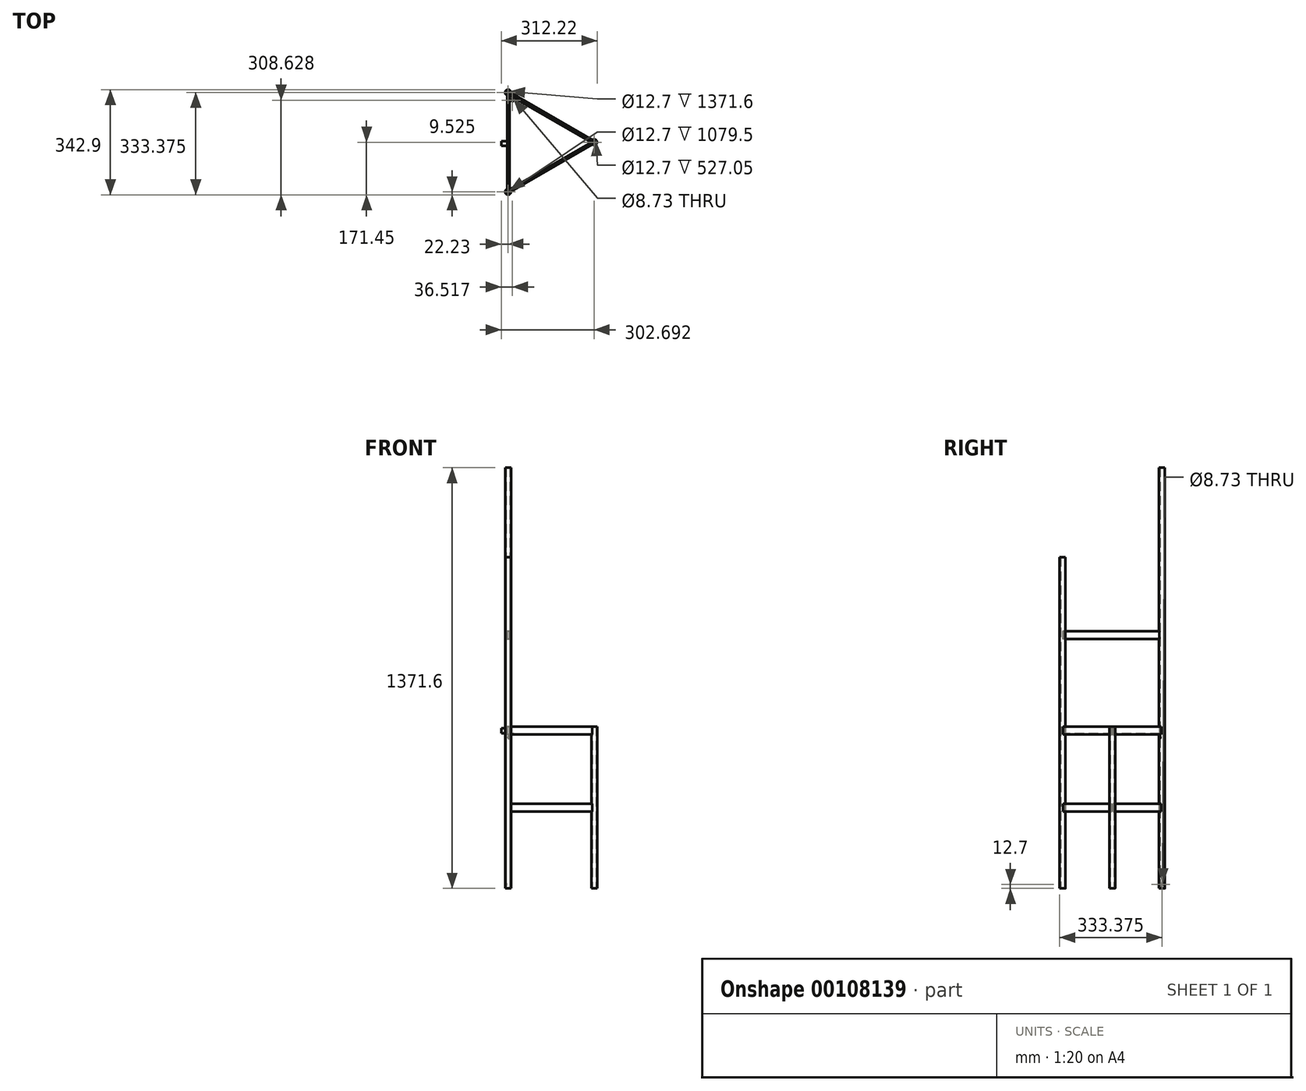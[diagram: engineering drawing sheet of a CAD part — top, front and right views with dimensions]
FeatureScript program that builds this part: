
annotation { "Feature Type Name" : "Feature", "Feature Type Description" : "" }
export const myFeature = defineFeature(function(context is Context, id is Id, definition is map)
    precondition{}
    {
        {
            var Q0;
            Q0=qCreatedBy(makeId("Top.planeOp"),FACE);
            var sketch = newSketch(context, id + "F0", { "sketchPlane" : qUnion([Q0])});
            skLineSegment(sketch, "E0.0", {"start": v(280.46, 0) * mm, "end": v(0, -161.92) * mm, "construction": true});
            skLineSegment(sketch, "E0.1", {"start": v(0, -161.93) * mm, "end": v(0, 161.92) * mm, "construction": true});
            skLineSegment(sketch, "E0.2", {"start": v(0, 161.93) * mm, "end": v(280.46, 0) * mm, "construction": true});
            skPoint(sketch, "E0.0.midPoint", {"position": v(140.23, -80.96) * mm});
            skCircle(sketch, "E1", {"center": v(0, 161.92) * mm, "radius": 9.52 * mm, "construction": true});
            skCircle(sketch, "E2", {"center": v(280.46, 0) * mm, "radius": 9.52 * mm, "construction": true});
            skCircle(sketch, "E3", {"center": v(0, -161.92) * mm, "radius": 9.52 * mm, "construction": true});
            skLineSegment(sketch, "E4", {"start": v(0, 0) * mm, "end": v(280.46, 0) * mm, "construction": true});
            skPoint(sketch, "E5", {"position": v(140.23, 80.96) * mm});
            skPoint(sketch, "E6", {"position": v(0, -152.4) * mm});
            skPoint(sketch, "E7", {"position": v(0, 152.4) * mm});
            skPoint(sketch, "E8", {"position": v(8.25, -157.16) * mm});
            skPoint(sketch, "E9", {"position": v(272.21, -4.76) * mm});
            skLineSegment(sketch, "E10", {"start": v(0, -161.92) * mm, "end": v(0, -171.45) * mm, "construction": true});
            skLineSegment(sketch, "E11", {"start": v(0, 161.92) * mm, "end": v(140.23, -80.96) * mm, "construction": true});
            skSolve(sketch);
        }
        {
            var Q0;
            Q0=qCreatedBy(makeId("Top.planeOp"),FACE);
            var sketch = newSketch(context, id + "F1", { "sketchPlane" : qUnion([Q0])});
            skCircle(sketch, "E12", {"center": v(0, 161.92) * mm, "radius": 9.52 * mm});
            skCircle(sketch, "E13.0", {"center": v(0, 161.92) * mm, "radius": 6.35 * mm});
            skSolve(sketch);
        }
        {
            var Q0;
            Q0 = qSketchRegion(id + "F1", true);
            extrude(context, id + "F2", {"entities" : qUnion([Q0]), "depth" : 1371.6 * mm});
        }
        {
            var Q0;
            Q0=qCreatedBy(makeId("Top.planeOp"),FACE);
            var sketch = newSketch(context, id + "F3", { "sketchPlane" : qUnion([Q0])});
            skCircle(sketch, "E14", {"center": v(0, -161.92) * mm, "radius": 9.52 * mm});
            skCircle(sketch, "E15.0", {"center": v(0, -161.92) * mm, "radius": 6.35 * mm});
            skSolve(sketch);
        }
        {
            var Q0;
            Q0 = qSketchRegion(id + "F3", true);
            extrude(context, id + "F4", {"entities" : qUnion([Q0]), "depth" : 1079.5 * mm});
        }
        {
            var Q0;
            Q0=qCreatedBy(makeId("Top.planeOp"),FACE);
            var sketch = newSketch(context, id + "F5", { "sketchPlane" : qUnion([Q0])});
            skCircle(sketch, "E16", {"center": v(280.46, 0) * mm, "radius": 9.52 * mm});
            skCircle(sketch, "E17.0", {"center": v(280.46, 0) * mm, "radius": 6.35 * mm});
            skSolve(sketch);
        }
        {
            var Q0;
            Q0 = qSketchRegion(id + "F5", true);
            extrude(context, id + "F6", {"entities" : qUnion([Q0]), "depth" : 527.05 * mm});
        }
        {
            var Q0;
            Q0=makeQuery(id+"F2.opExtrude","CAP_FACE",FACE,{"disambiguationData":[OSD([sQuery(id+"F1.wireOp",EDGE,"E12")])],"isStart":false});
            cPlane(context, id + "F7", {"entities" : qUnion([Q0]), "cplaneType" : CPlaneType.OFFSET, "offset" : 101.6 * mm, "width" : 152.4 * mm, "height" : 152.4 * mm});
        }
        {
            var Q0;
            Q0=qCreatedBy(id+"F7.planeOp",FACE);
            var sketch = newSketch(context, id + "F8", { "sketchPlane" : qUnion([Q0])});
            skArc(sketch, "E18", {"start": v(127, 161.92) * mm, "mid": v(0, 288.93) * mm, "end": v(-127, 161.93) * mm});
            skLineSegment(sketch, "E19", {"start": v(-127, 161.92) * mm, "end": v(127, 161.92) * mm});
            skLineSegment(sketch, "E20", {"start": v(127, 161.92) * mm, "end": v(165.16, 161.92) * mm, "construction": true});
            skSolve(sketch);
        }
        {
            var Q0;
            Q0 = qSketchRegion(id + "F8", true);
            var Q1;
            Q1=sQuery(id+"F8.wireOp",EDGE,"E19");
            revolve(context, id + "F9", {"entities" : qUnion([Q0]), "axis" : qUnion([Q1]), "revolveType" : RevolveType.FULL});
        }
        {
            var Q0;
            Q0=makeQuery(id+"F6.opExtrude","CAP_FACE",FACE,{"disambiguationData":[OSD([sQuery(id+"F5.wireOp",EDGE,"E16")])],"isStart":false});
            var sketch = newSketch(context, id + "F10", { "sketchPlane" : qUnion([Q0])});
            skCircle(sketch, "E21", {"center": v(156.83, 0) * mm, "radius": 215.9 * mm});
            skLineSegment(sketch, "E22.0", {"start": v(0, -161.93) * mm, "end": v(0, 161.92) * mm, "construction": true});
            skLineSegment(sketch, "E23", {"start": v(0, 0) * mm, "end": v(280.46, 0) * mm, "construction": true});
            skCircle(sketch, "E24.0", {"center": v(0, 161.92) * mm, "radius": 9.52 * mm, "construction": true});
            skSolve(sketch);
        }
        {
            var Q0;
            Q0 = qSketchRegion(id + "F10", true);
            extrude(context, id + "F11", {"entities" : qUnion([Q0]), "depth" : 19.05 * mm});
        }
        {
            var Q0;
            Q0=makeQuery(id+"F4.opExtrude","CAP_FACE",FACE,{"disambiguationData":[OSD([sQuery(id+"F3.wireOp",EDGE,"E14")])],"isStart":false});
            var sketch = newSketch(context, id + "F12", { "sketchPlane" : qUnion([Q0])});
            skLineSegment(sketch, "E25", {"start": v(0, -161.92) * mm, "end": v(0, -171.45) * mm, "construction": true});
            skLineSegment(sketch, "E26", {"start": v(0, -171.45) * mm, "end": v(0, -199.27) * mm, "construction": true});
            skSolve(sketch);
        }
        {
            var Q0;
            Q0=qCreatedBy(makeId("Right.planeOp"),FACE);
            var sketch = newSketch(context, id + "F13", { "sketchPlane" : qUnion([Q0])});
            skLineSegment(sketch, "E27.0", {"start": v(-161.92, 1079.5) * mm, "end": v(-171.45, 1079.5) * mm, "construction": true});
            skLineSegment(sketch, "E28", {"start": v(-72.12, 989.7) * mm, "end": v(-251.73, 1169.3) * mm});
            skLineSegment(sketch, "E29", {"start": v(-251.73, 1169.3) * mm, "end": v(-220.3, 1200.73) * mm});
            skLineSegment(sketch, "E30", {"start": v(-220.3, 1200.73) * mm, "end": v(-40.7, 1021.13) * mm});
            skLineSegment(sketch, "E31", {"start": v(-40.7, 1021.13) * mm, "end": v(-72.12, 989.7) * mm});
            skSolve(sketch);
        }
        {
            var Q0;
            Q0 = qSketchRegion(id + "F13", true);
            var Q1;
            Q1=sQuery(id+"F13.wireOp",EDGE,"E30");
            revolve(context, id + "F14", {"entities" : qUnion([Q0]), "axis" : qUnion([Q1]), "revolveType" : RevolveType.FULL});
        }
        {
            var Q0;
            Q0=qCreatedBy(makeId("Front.planeOp"),FACE);
            var Q1;
            Q1=sQuery(id+"F0.wireOp",VERTEX,"E10.start");
            cPlane(context, id + "F15", {"entities" : qUnion([Q0, Q1]), "cplaneType" : CPlaneType.PLANE_POINT, "offset" : 25.4 * mm, "width" : 152.4 * mm, "height" : 152.4 * mm});
        }
        {
            var Q0;
            Q0=qCreatedBy(id+"F15.planeOp",FACE);
            var sketch = newSketch(context, id + "F16", { "sketchPlane" : qUnion([Q0])});
            skLineSegment(sketch, "E32", {"start": v(0, 0) * mm, "end": v(0, -94.54) * mm, "construction": true});
            skSolve(sketch);
        }
        {
            var Q0;
            Q0=makeQuery(id+"F14.opRevolve","SWEPT_BODY",BODY,{"disambiguationData":[OSD([sQuery(id+"F13.wireOp",EDGE,"E28"),sQuery(id+"F13.wireOp",EDGE,"E29"),sQuery(id+"F13.wireOp",EDGE,"E30"),sQuery(id+"F13.wireOp",EDGE,"E31")])]});
            var Q1;
            Q1=sQuery(id+"F16.wireOp",EDGE,"E32");
            transform(context, id + "F17", {"entities" : qUnion([Q0]), "transformType" : TransformType.ROTATION, "transformAxis" : qUnion([Q1]), "angle" : 125 * degree, "makeCopy" : false});
        }
        {
            var Q0;
            Q0=qCreatedBy(makeId("Front.planeOp"),FACE);
            var sketch = newSketch(context, id + "F18", { "sketchPlane" : qUnion([Q0])});
            skCircle(sketch, "E33", {"center": v(0, 263.53) * mm, "radius": 9.53 * mm});
            skLineSegment(sketch, "E34", {"start": v(0, 0) * mm, "end": v(0, 527.05) * mm, "construction": true});
            skLineSegment(sketch, "E35.0", {"start": v(-59.07, 527.05) * mm, "end": v(372.73, 527.05) * mm, "construction": true});
            skSolve(sketch);
        }
        {
            var Q0;
            Q0 = qSketchRegion(id + "F18", true);
            var Q1;
            Q1=makeQuery(id+"F4.opExtrude","SWEPT_FACE",FACE,{"disambiguationData":[OSD([sQuery(id+"F3.wireOp",EDGE,"E14")])]});
            var Q2;
            Q2=makeQuery(id+"F2.opExtrude","SWEPT_FACE",FACE,{"disambiguationData":[OSD([sQuery(id+"F1.wireOp",EDGE,"E12")])]});
            extrude(context, id + "F19", {"entities" : qUnion([Q0]), "endBound" : BoundingType.UP_TO_SURFACE, "endBoundEntityFace" : qUnion([Q1]), "depth" : 25.4 * mm, "hasSecondDirection" : true, "secondDirectionBound" : BoundingType.UP_TO_SURFACE, "secondDirectionOppositeDirection" : true, "secondDirectionBoundEntityFace" : qUnion([Q2]), "secondDirectionDepth" : 25.4 * mm});
        }
        {
            var Q0;
            Q0=makeQuery(id+"F6.opExtrude","CAP_FACE",FACE,{"disambiguationData":[OSD([sQuery(id+"F5.wireOp",EDGE,"E16")])],"isStart":false});
            var sketch = newSketch(context, id + "F20", { "sketchPlane" : qUnion([Q0])});
            skCircle(sketch, "E36.0", {"center": v(280.46, 0) * mm, "radius": 9.52 * mm, "construction": true});
            skSolve(sketch);
        }
        {
            var Q0;
            Q0=sQuery(id+"F0.wireOp",EDGE,"E0.0");
            var Q1;
            Q1=sQuery(id+"F0.wireOp",VERTEX,"E0.0.midPoint");
            cPlane(context, id + "F21", {"entities" : qUnion([Q0, Q1]), "cplaneType" : CPlaneType.LINE_POINT, "offset" : 25.4 * mm, "width" : 152.4 * mm, "height" : 152.4 * mm});
        }
        {
            var Q0;
            Q0=sQuery(id+"F0.wireOp",EDGE,"E0.2");
            var Q1;
            Q1=sQuery(id+"F0.wireOp",VERTEX,"E5");
            cPlane(context, id + "F22", {"entities" : qUnion([Q0, Q1]), "cplaneType" : CPlaneType.LINE_POINT, "offset" : 25.4 * mm, "width" : 152.4 * mm, "height" : 152.4 * mm});
        }
        {
            var Q0;
            Q0=qCreatedBy(id+"F21.planeOp",FACE);
            var sketch = newSketch(context, id + "F23", { "sketchPlane" : qUnion([Q0])});
            skCircle(sketch, "E37", {"center": v(140.23, 263.53) * mm, "radius": 9.53 * mm, "construction": true});
            skLineSegment(sketch, "E38", {"start": v(140.23, 0) * mm, "end": v(140.23, 527.05) * mm, "construction": true});
            skLineSegment(sketch, "E39.bottom", {"start": v(143.4, 276.23) * mm, "end": v(137.06, 276.23) * mm});
            skLineSegment(sketch, "E39.top", {"start": v(143.4, 250.83) * mm, "end": v(137.06, 250.83) * mm});
            skLineSegment(sketch, "E39.left", {"start": v(143.4, 276.23) * mm, "end": v(143.4, 250.83) * mm});
            skLineSegment(sketch, "E39.right", {"start": v(137.06, 276.23) * mm, "end": v(137.06, 250.83) * mm});
            skLineSegment(sketch, "E40", {"start": v(137.06, 276.23) * mm, "end": v(143.4, 250.83) * mm, "construction": true});
            skLineSegment(sketch, "E41.bottom", {"start": v(137.06, 501.65) * mm, "end": v(143.4, 501.65) * mm});
            skLineSegment(sketch, "E41.top", {"start": v(137.06, 527.05) * mm, "end": v(143.4, 527.05) * mm});
            skLineSegment(sketch, "E41.left", {"start": v(137.06, 501.65) * mm, "end": v(137.06, 527.05) * mm});
            skLineSegment(sketch, "E41.right", {"start": v(143.4, 501.65) * mm, "end": v(143.4, 527.05) * mm});
            skPoint(sketch, "E41.middle", {"position": v(140.23, 514.35) * mm});
            skSolve(sketch);
        }
        {
            var Q0;
            Q0 = qSketchRegion(id + "F23", true);
            var Q1;
            Q1=makeQuery(id+"F4.opExtrude","SWEPT_FACE",FACE,{"disambiguationData":[OSD([sQuery(id+"F3.wireOp",EDGE,"E14")])]});
            var Q2;
            Q2=makeQuery(id+"F6.opExtrude","SWEPT_FACE",FACE,{"disambiguationData":[OSD([sQuery(id+"F5.wireOp",EDGE,"E16")])]});
            extrude(context, id + "F24", {"entities" : qUnion([Q0]), "endBound" : BoundingType.UP_TO_SURFACE, "endBoundEntityFace" : qUnion([Q1]), "depth" : 25.4 * mm, "hasSecondDirection" : true, "secondDirectionBound" : BoundingType.UP_TO_SURFACE, "secondDirectionOppositeDirection" : true, "secondDirectionBoundEntityFace" : qUnion([Q2]), "secondDirectionDepth" : 25.4 * mm});
        }
        {
            var Q0;
            Q0=qCreatedBy(id+"F22.planeOp",FACE);
            var sketch = newSketch(context, id + "F25", { "sketchPlane" : qUnion([Q0])});
            skLineSegment(sketch, "E42", {"start": v(140.23, 0) * mm, "end": v(140.23, 527.05) * mm, "construction": true});
            skCircle(sketch, "E43", {"center": v(140.23, 263.53) * mm, "radius": 9.53 * mm, "construction": true});
            skLineSegment(sketch, "E44.bottom", {"start": v(137.06, 250.83) * mm, "end": v(143.4, 250.83) * mm});
            skLineSegment(sketch, "E44.top", {"start": v(137.06, 276.23) * mm, "end": v(143.4, 276.23) * mm});
            skLineSegment(sketch, "E44.left", {"start": v(137.06, 250.83) * mm, "end": v(137.06, 276.23) * mm});
            skLineSegment(sketch, "E44.right", {"start": v(143.4, 250.83) * mm, "end": v(143.4, 276.23) * mm});
            skLineSegment(sketch, "E45", {"start": v(143.4, 276.23) * mm, "end": v(137.06, 250.83) * mm, "construction": true});
            skLineSegment(sketch, "E46.bottom", {"start": v(143.4, 527.05) * mm, "end": v(137.06, 527.05) * mm});
            skLineSegment(sketch, "E46.top", {"start": v(143.4, 501.65) * mm, "end": v(137.06, 501.65) * mm});
            skLineSegment(sketch, "E46.left", {"start": v(143.4, 527.05) * mm, "end": v(143.4, 501.65) * mm});
            skLineSegment(sketch, "E46.right", {"start": v(137.06, 527.05) * mm, "end": v(137.06, 501.65) * mm});
            skPoint(sketch, "E46.middle", {"position": v(140.23, 514.35) * mm});
            skSolve(sketch);
        }
        {
            var Q0;
            Q0 = qSketchRegion(id + "F25", true);
            var Q1;
            Q1=makeQuery(id+"F6.opExtrude","SWEPT_FACE",FACE,{"disambiguationData":[OSD([sQuery(id+"F5.wireOp",EDGE,"E16")])]});
            var Q2;
            Q2=makeQuery(id+"F2.opExtrude","SWEPT_FACE",FACE,{"disambiguationData":[OSD([sQuery(id+"F1.wireOp",EDGE,"E12")])]});
            extrude(context, id + "F26", {"entities" : qUnion([Q0]), "endBound" : BoundingType.UP_TO_SURFACE, "endBoundEntityFace" : qUnion([Q1]), "depth" : 25.4 * mm, "hasSecondDirection" : true, "secondDirectionBound" : BoundingType.UP_TO_SURFACE, "secondDirectionOppositeDirection" : true, "secondDirectionBoundEntityFace" : qUnion([Q2]), "secondDirectionDepth" : 25.4 * mm});
        }
        {
            var Q0;
            Q0=makeQuery(id+"F24.opExtrude","SWEPT_FACE",FACE,{"disambiguationData":[OSD([sQuery(id+"F23.wireOp",EDGE,"E41.bottom")])]});
            var sketch = newSketch(context, id + "F27", { "sketchPlane" : qUnion([Q0])});
            skLineSegment(sketch, "E47.0", {"start": v(280.46, 0) * mm, "end": v(0, 161.92) * mm, "construction": true});
            skLineSegment(sketch, "E47.1", {"start": v(0, -161.93) * mm, "end": v(280.46, 0) * mm, "construction": true});
            skLineSegment(sketch, "E47.2", {"start": v(0, 161.93) * mm, "end": v(0, -161.92) * mm, "construction": true});
            skLineSegment(sketch, "E48.0", {"start": v(270.94, 0) * mm, "end": v(4.76, 153.68) * mm});
            skLineSegment(sketch, "E48.1", {"start": v(4.76, -153.68) * mm, "end": v(270.94, 0) * mm});
            skLineSegment(sketch, "E48.2", {"start": v(4.76, 153.68) * mm, "end": v(4.76, -153.68) * mm});
            skCircle(sketch, "E49.0", {"center": v(0, 161.92) * mm, "radius": 9.52 * mm, "construction": true});
            skCircle(sketch, "E49.1", {"center": v(280.46, 0) * mm, "radius": 9.52 * mm, "construction": true});
            skCircle(sketch, "E49.2", {"center": v(0, -161.92) * mm, "radius": 9.52 * mm, "construction": true});
            skSolve(sketch);
        }
        {
            var Q0;
            {var subQ0=sQuery(id+"F27.wireOp",EDGE,"E48.0");var subQ5=sQuery(id+"F27.wireOp",EDGE,"E48.1");var subQ6=makeQuery(id+"F27.imprint","INTERSECT",VERTEX,{"derivedFrom":[subQ0,subQ5]});Q0=makeQuery(id+"F27.imprint","IMPRINT",FACE,{"disambiguationData":[TD([[makeQuery(id+"F27.imprint","IMPRINT",EDGE,{"disambiguationData":[TD([[subQ6,-1.0]])],"derivedFrom":subQ0}),1.0]])]});}
            extrude(context, id + "F28", {"entities" : qUnion([Q0]), "oppositeDirection" : true, "depth" : 3.17 * mm});
        }
        {
            var Q0;
            Q0=qCreatedBy(id+"F15.planeOp",FACE);
            var sketch = newSketch(context, id + "F29", { "sketchPlane" : qUnion([Q0])});
            skLineSegment(sketch, "E50.0", {"start": v(-9.53, 0) * mm, "end": v(9.52, 0) * mm, "construction": true});
            skLineSegment(sketch, "E51", {"start": v(-9.53, 0) * mm, "end": v(-9.53, 527.05) * mm, "construction": true});
            skLineSegment(sketch, "E52.0", {"start": v(-59.07, 527.05) * mm, "end": v(372.73, 527.05) * mm, "construction": true});
            skLineSegment(sketch, "E53", {"start": v(9.52, 0) * mm, "end": v(9.52, 527.05) * mm, "construction": true});
            skCircle(sketch, "E54", {"center": v(0, 517.52) * mm, "radius": 9.52 * mm, "construction": true});
            skLineSegment(sketch, "E55.bottom", {"start": v(3.17, 527.05) * mm, "end": v(-3.18, 527.05) * mm});
            skLineSegment(sketch, "E55.top", {"start": v(3.17, 501.65) * mm, "end": v(-3.18, 501.65) * mm});
            skLineSegment(sketch, "E55.left", {"start": v(-3.18, 501.65) * mm, "end": v(-3.18, 527.05) * mm});
            skLineSegment(sketch, "E55.right", {"start": v(3.17, 501.65) * mm, "end": v(3.17, 527.05) * mm});
            skPoint(sketch, "E55.middle", {"position": v(0, 514.35) * mm});
            skSolve(sketch);
        }
        {
            var Q0;
            Q0 = qSketchRegion(id + "F29", true);
            var Q1;
            Q1=makeQuery(id+"F2.opExtrude","SWEPT_FACE",FACE,{"disambiguationData":[OSD([sQuery(id+"F1.wireOp",EDGE,"E12")])]});
            extrude(context, id + "F30", {"entities" : qUnion([Q0]), "endBound" : BoundingType.UP_TO_SURFACE, "oppositeDirection" : true, "endBoundEntityFace" : qUnion([Q1]), "depth" : 25.4 * mm});
        }
        {
            var Q0;
            Q0=qCreatedBy(makeId("Right.planeOp"),FACE);
            var sketch = newSketch(context, id + "F31", { "sketchPlane" : qUnion([Q0])});
            skLineSegment(sketch, "E56.0", {"start": v(152.4, 1371.6) * mm, "end": v(171.45, 1371.6) * mm, "construction": true});
            skLineSegment(sketch, "E57.bottom", {"start": v(104.77, 1381.13) * mm, "end": v(219.07, 1381.13) * mm, "construction": true});
            skLineSegment(sketch, "E57.top", {"start": v(104.77, 1371.6) * mm, "end": v(219.08, 1371.6) * mm, "construction": true});
            skLineSegment(sketch, "E57.left", {"start": v(104.77, 1381.13) * mm, "end": v(104.77, 1371.6) * mm, "construction": true});
            skLineSegment(sketch, "E57.right", {"start": v(219.07, 1381.13) * mm, "end": v(219.07, 1371.6) * mm, "construction": true});
            skPoint(sketch, "E58", {"position": v(161.92, 1371.6) * mm});
            skCircle(sketch, "E59", {"center": v(161.92, 1494.54) * mm, "radius": 127 * mm, "construction": true});
            skPoint(sketch, "E59.centerSnap0", {"position": v(161.92, 1381.13) * mm});
            skSolve(sketch);
        }
        {
            var Q0;
            Q0=qCreatedBy(makeId("Right.planeOp"),FACE);
            var sketch = newSketch(context, id + "F32", { "sketchPlane" : qUnion([Q0])});
            skLineSegment(sketch, "E60.0", {"start": v(104.77, 1381.13) * mm, "end": v(219.07, 1381.13) * mm, "construction": true});
            skLineSegment(sketch, "E60.1", {"start": v(104.77, 1371.6) * mm, "end": v(219.08, 1371.6) * mm, "construction": true});
            skLineSegment(sketch, "E61.bottom", {"start": v(161.92, 1381.13) * mm, "end": v(219.07, 1381.13) * mm});
            skLineSegment(sketch, "E61.top", {"start": v(161.92, 1371.6) * mm, "end": v(219.08, 1371.6) * mm});
            skLineSegment(sketch, "E61.left", {"start": v(161.92, 1381.13) * mm, "end": v(161.92, 1371.6) * mm});
            skLineSegment(sketch, "E61.right", {"start": v(219.07, 1381.13) * mm, "end": v(219.07, 1371.6) * mm});
            skLineSegment(sketch, "E62", {"start": v(161.92, 1381.13) * mm, "end": v(161.92, 1410.8) * mm, "construction": true});
            skSolve(sketch);
        }
        {
            var Q0;
            Q0=makeQuery(id+"F32.imprint","IMPRINT",FACE,{"disambiguationData":[TD([[makeQuery(id+"F32.imprint","IMPRINT",EDGE,{"derivedFrom":sQuery(id+"F32.wireOp",EDGE,"E61.bottom")}),-1.0]])]});
            var Q1;
            Q1=sQuery(id+"F32.wireOp",EDGE,"E62");
            revolve(context, id + "F33", {"entities" : qUnion([Q0]), "axis" : qUnion([Q1]), "revolveType" : RevolveType.FULL});
        }
        {
            var Q0;
            Q0=qCreatedBy(makeId("Right.planeOp"),FACE);
            var sketch = newSketch(context, id + "F34", { "sketchPlane" : qUnion([Q0])});
            skArc(sketch, "E63.0", {"start": v(212.73, 1378.14) * mm, "mid": v(286.25, 1520.49) * mm, "end": v(161.92, 1621.54) * mm});
            skLineSegment(sketch, "E64.0", {"start": v(161.92, 1381.13) * mm, "end": v(219.07, 1381.13) * mm, "construction": true});
            skLineSegment(sketch, "E65", {"start": v(161.92, 1381.13) * mm, "end": v(161.92, 1494.54) * mm, "construction": true});
            skPoint(sketch, "E66.orphan", {"position": v(104.77, 1381.13) * mm});
            skArc(sketch, "E67.0", {"start": v(212.72, 1381.61) * mm, "mid": v(283, 1520.52) * mm, "end": v(161.92, 1618.36) * mm});
            skLineSegment(sketch, "E68.trimOffspring", {"start": v(161.92, 1618.36) * mm, "end": v(161.92, 1621.54) * mm});
            skCircle(sketch, "E69.0", {"center": v(161.92, 1494.54) * mm, "radius": 127 * mm, "construction": true});
            skLineSegment(sketch, "E70.0", {"start": v(212.72, 1378.14) * mm, "end": v(212.72, 1513.56) * mm, "construction": true});
            skLineSegment(sketch, "E71", {"start": v(212.72, 1381.61) * mm, "end": v(212.72, 1378.14) * mm});
            skSolve(sketch);
        }
        {
            var Q0;
            Q0 = qSketchRegion(id + "F34", true);
            var Q1;
            Q1=sQuery(id+"F34.wireOp",EDGE,"E65");
            revolve(context, id + "F35", {"entities" : qUnion([Q0]), "axis" : qUnion([Q1]), "revolveType" : RevolveType.FULL});
        }
        {
            var Q0;
            Q0=qCreatedBy(id+"F15.planeOp",FACE);
            var sketch = newSketch(context, id + "F36", { "sketchPlane" : qUnion([Q0])});
            skLineSegment(sketch, "E72.0", {"start": v(-9.52, 0) * mm, "end": v(9.53, 0) * mm, "construction": true});
            skCircle(sketch, "E73", {"center": v(0, 825.5) * mm, "radius": 9.52 * mm, "construction": true});
            skLineSegment(sketch, "E74", {"start": v(9.52, 825.5) * mm, "end": v(-9.52, 825.5) * mm, "construction": true});
            skLineSegment(sketch, "E75.0", {"start": v(-9.52, 1079.5) * mm, "end": v(9.52, 1079.5) * mm, "construction": true});
            skLineSegment(sketch, "E76.1", {"start": v(-59.07, 546.1) * mm, "end": v(372.73, 546.1) * mm, "construction": true});
            skLineSegment(sketch, "E77", {"start": v(0, 546.1) * mm, "end": v(0, 1079.5) * mm, "construction": true});
            skLineSegment(sketch, "E78.bottom", {"start": v(3.18, 838.2) * mm, "end": v(-3.17, 838.2) * mm});
            skLineSegment(sketch, "E78.top", {"start": v(3.18, 812.8) * mm, "end": v(-3.17, 812.8) * mm});
            skLineSegment(sketch, "E78.right", {"start": v(-3.17, 838.2) * mm, "end": v(-3.17, 812.8) * mm});
            skLineSegment(sketch, "E79.top", {"start": v(7.92, 825.5) * mm, "end": v(7.92, 825.5) * mm});
            skLineSegment(sketch, "E80", {"start": v(3.18, 838.2) * mm, "end": v(3.18, 812.8) * mm});
            skLineSegment(sketch, "E81", {"start": v(-3.17, 838.2) * mm, "end": v(3.18, 812.8) * mm, "construction": true});
            skPoint(sketch, "E82", {"position": v(0, 812.8) * mm});
            skLineSegment(sketch, "E83.0", {"start": v(6.19, 276.23) * mm, "end": v(271.1, 276.23) * mm, "construction": true});
            skLineSegment(sketch, "E83.1", {"start": v(9.36, 250.83) * mm, "end": v(274.27, 250.83) * mm, "construction": true});
            skLineSegment(sketch, "E83.2", {"start": v(9.36, 501.65) * mm, "end": v(274.27, 501.65) * mm, "construction": true});
            skLineSegment(sketch, "E84", {"start": v(274.32, 504.83) * mm, "end": v(271.1, 276.22) * mm, "construction": true});
            skLineSegment(sketch, "E85", {"start": v(0, 546.1) * mm, "end": v(0, 825.5) * mm});
            skLineSegment(sketch, "E86", {"start": v(372.73, 546.1) * mm, "end": v(372.73, 825.5) * mm, "construction": true});
            skLineSegment(sketch, "E87.0", {"start": v(270.94, 504.83) * mm, "end": v(270.94, 504.83) * mm});
            skSolve(sketch);
        }
        {
            var Q0;
            Q0 = qSketchRegion(id + "F36", true);
            var Q1;
            Q1=makeQuery(id+"F2.opExtrude","SWEPT_FACE",FACE,{"disambiguationData":[OSD([sQuery(id+"F1.wireOp",EDGE,"E12")])]});
            extrude(context, id + "F37", {"entities" : qUnion([Q0]), "endBound" : BoundingType.UP_TO_SURFACE, "oppositeDirection" : true, "endBoundEntityFace" : qUnion([Q1]), "depth" : 25.4 * mm});
        }
        {
            var Q0;
            Q0=makeQuery(id+"F12.imprint","IMPRINT",FACE,{"disambiguationData":[TD([[makeQuery(id+"F12.imprint","IMPRINT",EDGE,{"derivedFrom":makeQuery(id+"F4.opExtrude","CAP_EDGE",EDGE,{"disambiguationData":[OSD([sQuery(id+"F3.wireOp",EDGE,"E14")])],"isStart":false})}),1.0]])]});
            var sketch = newSketch(context, id + "F38", { "sketchPlane" : qUnion([Q0])});
            skCircle(sketch, "E88.0", {"center": v(0, -161.92) * mm, "radius": 9.52 * mm});
            skSolve(sketch);
        }
        {
            var Q0;
            Q0=makeQuery(id+"F9.opRevolve","SWEPT_BODY",BODY,{"disambiguationData":[OSD([sQuery(id+"F8.wireOp",EDGE,"E18"),sQuery(id+"F8.wireOp",EDGE,"E19")])]});
            deleteBodies(context, id + "F39", {"entities" : qUnion([Q0])});
        }
        {
            var Q0;
            Q0=makeQuery(id+"F14.opRevolve","SWEPT_BODY",BODY,{"disambiguationData":[OSD([sQuery(id+"F13.wireOp",EDGE,"E28"),sQuery(id+"F13.wireOp",EDGE,"E29"),sQuery(id+"F13.wireOp",EDGE,"E30"),sQuery(id+"F13.wireOp",EDGE,"E31")])]});
            var Q1;
            Q1=makeQuery(id+"F19.opExtrude","SWEPT_BODY",BODY,{"disambiguationData":[OSD([sQuery(id+"F18.wireOp",EDGE,"E33")])]});
            deleteBodies(context, id + "F40", {"entities" : qUnion([Q0, Q1])});
        }
        {
            var Q0;
            Q0=makeQuery(id+"F30.opExtrude","SWEPT_BODY",BODY,{"disambiguationData":[OSD([sQuery(id+"F29.wireOp",EDGE,"E55.bottom"),sQuery(id+"F29.wireOp",EDGE,"E55.top"),sQuery(id+"F29.wireOp",EDGE,"E55.left"),sQuery(id+"F29.wireOp",EDGE,"E55.right")])]});
            var Q1;
            Q1=makeQuery(id+"F6.opExtrude","SWEPT_BODY",BODY,{"disambiguationData":[OSD([sQuery(id+"F5.wireOp",EDGE,"E16")])]});
            var Q2;
            Q2=makeQuery(id+"F24.opExtrude","SWEPT_BODY",BODY,{"disambiguationData":[OSD([sQuery(id+"F23.wireOp",EDGE,"E41.bottom"),sQuery(id+"F23.wireOp",EDGE,"E41.top"),sQuery(id+"F23.wireOp",EDGE,"E41.left"),sQuery(id+"F23.wireOp",EDGE,"E41.right")])]});
            var Q3;
            Q3=makeQuery(id+"F26.opExtrude","SWEPT_BODY",BODY,{"disambiguationData":[OSD([sQuery(id+"F25.wireOp",EDGE,"E46.bottom"),sQuery(id+"F25.wireOp",EDGE,"E46.top"),sQuery(id+"F25.wireOp",EDGE,"E46.left"),sQuery(id+"F25.wireOp",EDGE,"E46.right")])]});
            var Q4;
            Q4=makeQuery(id+"F24.opExtrude","SWEPT_BODY",BODY,{"disambiguationData":[OSD([sQuery(id+"F23.wireOp",EDGE,"E39.bottom"),sQuery(id+"F23.wireOp",EDGE,"E39.top"),sQuery(id+"F23.wireOp",EDGE,"E39.left"),sQuery(id+"F23.wireOp",EDGE,"E39.right")])]});
            var Q5;
            Q5=makeQuery(id+"F26.opExtrude","SWEPT_BODY",BODY,{"disambiguationData":[OSD([sQuery(id+"F25.wireOp",EDGE,"E44.bottom"),sQuery(id+"F25.wireOp",EDGE,"E44.top"),sQuery(id+"F25.wireOp",EDGE,"E44.left"),sQuery(id+"F25.wireOp",EDGE,"E44.right")])]});
            var Q6;
            Q6=makeQuery(id+"F2.opExtrude","SWEPT_BODY",BODY,{"disambiguationData":[OSD([sQuery(id+"F1.wireOp",EDGE,"E12")])]});
            var Q7;
            Q7=makeQuery(id+"F4.opExtrude","SWEPT_BODY",BODY,{"disambiguationData":[OSD([sQuery(id+"F3.wireOp",EDGE,"E14")])]});
            var Q8;
            Q8=makeQuery(id+"Fk7LuZj7NATegNz_11.opExtrude","SWEPT_BODY",BODY,{"disambiguationData":[OSD([sQuery(id+"F38.wireOp",EDGE,"E88.0")])]});
            var Q9;
            Q9=makeQuery(id+"F37.opExtrude","SWEPT_BODY",BODY,{"disambiguationData":[OSD([sQuery(id+"F36.wireOp",EDGE,"E78.bottom"),sQuery(id+"F36.wireOp",EDGE,"E78.top"),sQuery(id+"F36.wireOp",EDGE,"E78.right"),sQuery(id+"F36.wireOp",EDGE,"E80")])]});
            booleanBodies(context, id + "F41", {"operationType" : BooleanOperationType.UNION, "tools" : qUnion([Q0, Q1, Q2, Q3, Q4, Q5, Q6, Q7, Q8, Q9])});
        }
        {
            var Q0;
            Q0=qCreatedBy(makeId("Right.planeOp"),FACE);
            var sketch = newSketch(context, id + "F42", { "sketchPlane" : qUnion([Q0])});
            skLineSegment(sketch, "E89.0", {"start": v(152.4, 0) * mm, "end": v(171.45, 0) * mm, "construction": true});
            skCircle(sketch, "E90", {"center": v(161.92, 12.7) * mm, "radius": 4.37 * mm});
            skPoint(sketch, "E90.centerSnap0", {"position": v(161.92, 0) * mm});
            skSolve(sketch);
        }
        {
            var Q0;
            Q0 = qSketchRegion(id + "F42", true);
            extrude(context, id + "F43", {"entities" : qUnion([Q0]), "operationType" : NewBodyOperationType.REMOVE, "oppositeDirection" : true, "depth" : 25.4 * mm});
        }
        {
            var Q0;
            Q0=sQuery(id+"F0.wireOp",VERTEX,"E1.center");
            var Q1;
            Q1=sQuery(id+"F0.wireOp",EDGE,"E11");
            cPlane(context, id + "F44", {"entities" : qUnion([Q0, Q1]), "cplaneType" : CPlaneType.LINE_POINT, "offset" : 25.4 * mm, "width" : 152.4 * mm, "height" : 152.4 * mm});
        }
        {
            var Q0;
            Q0=qCreatedBy(id+"F44.planeOp",FACE);
            var sketch = newSketch(context, id + "F45", { "sketchPlane" : qUnion([Q0])});
            skLineSegment(sketch, "E91.0", {"start": v(71.44, 0) * mm, "end": v(90.49, 0) * mm, "construction": true});
            skCircle(sketch, "E92", {"center": v(80.96, 492.13) * mm, "radius": 4.37 * mm});
            skPoint(sketch, "E92.centerSnap0", {"position": v(80.96, 0) * mm});
            skLineSegment(sketch, "E93.0", {"start": v(82.7, 501.65) * mm, "end": v(88.2, 501.65) * mm, "construction": true});
            skSolve(sketch);
        }
        {
            var Q0;
            Q0 = qSketchRegion(id + "F45", true);
            var Q1;
            Q1=makeQuery(id+"F2.opExtrude","SWEPT_FACE",FACE,{"disambiguationData":[OSD([sQuery(id+"F1.wireOp",EDGE,"E12")])]});
            extrude(context, id + "F46", {"entities" : qUnion([Q0]), "operationType" : NewBodyOperationType.REMOVE, "endBound" : BoundingType.UP_TO_SURFACE, "endBoundEntityFace" : qUnion([Q1]), "depth" : 25.4 * mm});
        }
        {
            var Q0;
            Q0=makeQuery(id+"F28.opExtrude","CAP_FACE",FACE,{"disambiguationData":[OSD([sQuery(id+"F27.wireOp",EDGE,"E48.0"),sQuery(id+"F27.wireOp",EDGE,"E48.1"),sQuery(id+"F27.wireOp",EDGE,"E48.2")])],"isStart":false});
            var sketch = newSketch(context, id + "F47", { "sketchPlane" : qUnion([Q0])});
            skLineSegment(sketch, "E94.1", {"start": v(4.76, -153.68) * mm, "end": v(4.76, 153.68) * mm, "construction": true});
            skLineSegment(sketch, "E94.2", {"start": v(270.94, 0) * mm, "end": v(4.76, -153.68) * mm, "construction": true});
            skLineSegment(sketch, "E95.0", {"start": v(4.76, 153.68) * mm, "end": v(270.94, 0) * mm, "construction": true});
            skLineSegment(sketch, "E96.0", {"start": v(251.89, 0) * mm, "end": v(14.29, 137.18) * mm, "construction": true});
            skLineSegment(sketch, "E96.1", {"start": v(14.29, -137.18) * mm, "end": v(251.89, 0) * mm, "construction": true});
            skLineSegment(sketch, "E96.2", {"start": v(14.29, 137.18) * mm, "end": v(14.29, -137.18) * mm, "construction": true});
            skCircle(sketch, "E97", {"center": v(14.29, 137.18) * mm, "radius": 4.37 * mm});
            skSolve(sketch);
        }
        {
            var Q0;
            Q0 = qSketchRegion(id + "F47", true);
            var Q1;
            Q1=makeQuery(id+"F28.opExtrude","CAP_FACE",FACE,{"disambiguationData":[OSD([sQuery(id+"F27.wireOp",EDGE,"E48.0"),sQuery(id+"F27.wireOp",EDGE,"E48.1"),sQuery(id+"F27.wireOp",EDGE,"E48.2")])],"isStart":true});
            extrude(context, id + "F48", {"entities" : qUnion([Q0]), "operationType" : NewBodyOperationType.REMOVE, "endBound" : BoundingType.UP_TO_SURFACE, "oppositeDirection" : true, "endBoundEntityFace" : qUnion([Q1]), "depth" : 25.4 * mm});
        }
        {
            var Q0;
            Q0=qCreatedBy(id+"F15.planeOp",FACE);
            var sketch = newSketch(context, id + "F49", { "sketchPlane" : qUnion([Q0])});
            skLineSegment(sketch, "E98.0", {"start": v(-9.52, 1079.5) * mm, "end": v(9.52, 1079.5) * mm, "construction": true});
            skLineSegment(sketch, "E99.0", {"start": v(-9.52, 1111.25) * mm, "end": v(9.52, 1111.25) * mm, "construction": true});
            skPoint(sketch, "E100.middle.positionSnap0", {"position": v(0, 1111.25) * mm});
            skPoint(sketch, "E100.centerSnap0", {"position": v(0, 1111.25) * mm});
            skLineSegment(sketch, "E101", {"start": v(-100.46, 1174.75) * mm, "end": v(119.51, 1047.75) * mm, "construction": true});
            skLineSegment(sketch, "E102", {"start": v(119.51, 1047.75) * mm, "end": v(141.74, 1086.24) * mm, "construction": true});
            skLineSegment(sketch, "E103", {"start": v(-100.46, 1174.75) * mm, "end": v(-78.24, 1213.24) * mm, "construction": true});
            skLineSegment(sketch, "E104", {"start": v(-56.01, 1251.74) * mm, "end": v(163.96, 1124.74) * mm});
            skPoint(sketch, "E105", {"position": v(9.52, 1111.25) * mm});
            skLineSegment(sketch, "E106", {"start": v(-78.24, 1213.24) * mm, "end": v(141.74, 1086.24) * mm, "construction": true});
            skLineSegment(sketch, "E107", {"start": v(-56.01, 1251.74) * mm, "end": v(-57.6, 1249) * mm, "construction": true});
            skLineSegment(sketch, "E108", {"start": v(162.37, 1122) * mm, "end": v(163.96, 1124.74) * mm, "construction": true});
            skLineSegment(sketch, "E109", {"start": v(-57.6, 1249) * mm, "end": v(-56.01, 1251.74) * mm});
            skLineSegment(sketch, "E110", {"start": v(163.96, 1124.74) * mm, "end": v(162.37, 1122) * mm});
            skLineSegment(sketch, "E111.0", {"start": v(-57.6, 1249) * mm, "end": v(162.37, 1122) * mm});
            skLineSegment(sketch, "E112.trimOffspring", {"start": v(-57.6, 1249) * mm, "end": v(-56.01, 1251.74) * mm, "construction": true});
            skSolve(sketch);
        }
        {
            var Q0;
            Q0 = qSketchRegion(id + "F49", true);
            var Q1;
            Q1=sQuery(id+"F49.wireOp",EDGE,"E106");
            revolve(context, id + "F50", {"entities" : qUnion([Q0]), "axis" : qUnion([Q1]), "revolveType" : RevolveType.FULL});
        }
        {
            var Q0;
            Q0=qCreatedBy(id+"F15.planeOp",FACE);
            var sketch = newSketch(context, id + "F51", { "sketchPlane" : qUnion([Q0])});
            skPoint(sketch, "E113.0", {"position": v(0, 0) * mm});
            skLineSegment(sketch, "E114", {"start": v(0, 0) * mm, "end": v(0, -16.7) * mm, "construction": true});
            skSolve(sketch);
        }
        {
            var Q0;
            Q0=makeQuery(id+"F50.opRevolve","SWEPT_BODY",BODY,{"disambiguationData":[OSD([sQuery(id+"F49.wireOp",EDGE,"E104"),sQuery(id+"F49.wireOp",EDGE,"E106"),sQuery(id+"F49.wireOp",EDGE,"E109"),sQuery(id+"F49.wireOp",EDGE,"E110")])]});
            var Q1;
            Q1=sQuery(id+"F51.wireOp",EDGE,"E114");
            transform(context, id + "F52", {"entities" : qUnion([Q0]), "transformType" : TransformType.ROTATION, "transformAxis" : qUnion([Q1]), "angle" : 35 * degree, "makeCopy" : false});
        }
        {
            var Q0;
            Q0=makeQuery(id+"F41.opBoolean","SPLIT",FACE,{"disambiguationData":[TD([makeQuery(id+"F2.opExtrude","SWEPT_FACE",FACE,{"disambiguationData":[OSD([sQuery(id+"F1.wireOp",EDGE,"E12")])]})])],"derivedFrom":makeQuery(id+"F30.opExtrude","SWEPT_FACE",FACE,{"disambiguationData":[OSD([sQuery(id+"F29.wireOp",EDGE,"E55.left")])]})});
            var sketch = newSketch(context, id + "F53", { "sketchPlane" : qUnion([Q0])});
            skLineSegment(sketch, "E115.0", {"start": v(-152.94, 501.65) * mm, "end": v(152.94, 501.65) * mm, "construction": true});
            skLineSegment(sketch, "E115.1", {"start": v(-215.9, 527.05) * mm, "end": v(215.9, 527.05) * mm, "construction": true});
            skLineSegment(sketch, "E116", {"start": v(4, 527.05) * mm, "end": v(4, 501.65) * mm, "construction": true});
            skCircle(sketch, "E117", {"center": v(4, 514.35) * mm, "radius": 7.94 * mm});
            skSolve(sketch);
        }
        {
            var Q0;
            Q0 = qSketchRegion(id + "F53", true);
            extrude(context, id + "F54", {"entities" : qUnion([Q0]), "depth" : 19.05 * mm});
        }
        {
            var Q0;
            Q0=makeQuery(id+"F11.opExtrude","SWEPT_BODY",BODY,{"disambiguationData":[OSD([sQuery(id+"F10.wireOp",EDGE,"E21")])]});
            var Q1;
            Q1=makeQuery(id+"F35.opRevolve","SWEPT_BODY",BODY,{"disambiguationData":[OSD([sQuery(id+"F34.wireOp",EDGE,"E63.0"),sQuery(id+"F34.wireOp",EDGE,"E67.0"),sQuery(id+"F34.wireOp",EDGE,"E68.trimOffspring"),sQuery(id+"F34.wireOp",EDGE,"E71")])]});
            var Q2;
            Q2=makeQuery(id+"F33.opRevolve","SWEPT_BODY",BODY,{"disambiguationData":[OSD([sQuery(id+"F32.wireOp",EDGE,"E61.bottom"),sQuery(id+"F32.wireOp",EDGE,"E61.top"),sQuery(id+"F32.wireOp",EDGE,"E61.left"),sQuery(id+"F32.wireOp",EDGE,"E61.right")])]});
            var Q3;
            Q3=makeQuery(id+"F50.opRevolve","SWEPT_BODY",BODY,{"disambiguationData":[OSD([sQuery(id+"F49.wireOp",EDGE,"E104"),sQuery(id+"F49.wireOp",EDGE,"E106"),sQuery(id+"F49.wireOp",EDGE,"E109"),sQuery(id+"F49.wireOp",EDGE,"E110")])]});
            deleteBodies(context, id + "F55", {"entities" : qUnion([Q0, Q1, Q2, Q3])});
        }
    });
